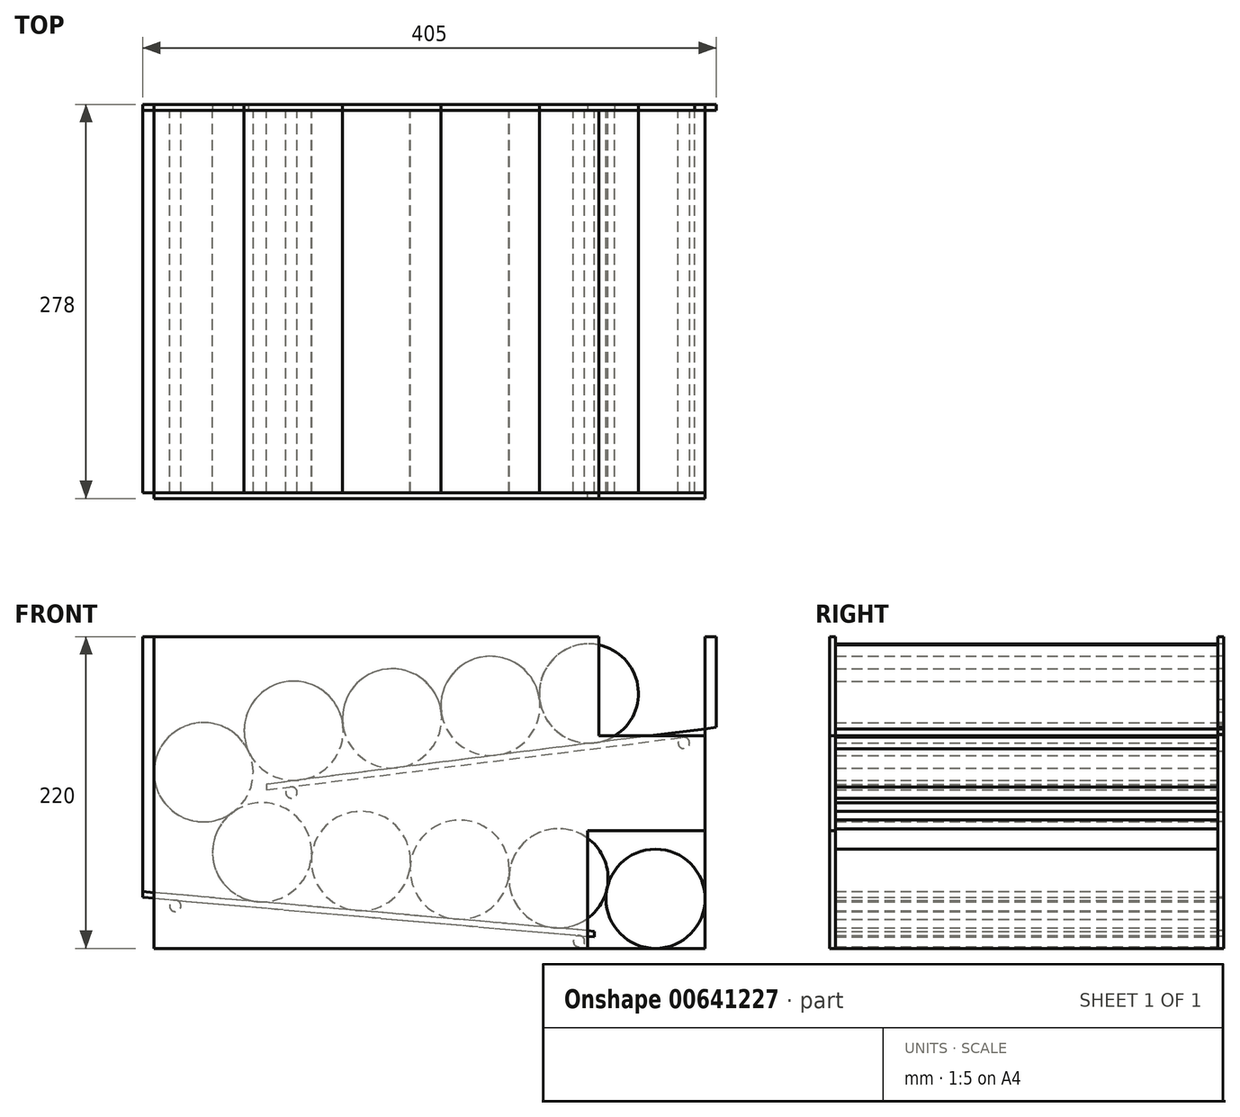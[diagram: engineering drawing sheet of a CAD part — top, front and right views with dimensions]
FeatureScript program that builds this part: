
annotation { "Feature Type Name" : "Feature", "Feature Type Description" : "" }
export const myFeature = defineFeature(function(context is Context, id is Id, definition is map)
    precondition{}
    {
        {
            var Q0;
            Q0=qCreatedBy(makeId("Front.planeOp"),FACE);
            var sketch = newSketch(context, id + "F0", { "sketchPlane" : qUnion([Q0])});
            skLineSegment(sketch, "E0.bottom", {"start": v(0, 0) * mm, "end": v(-405, 0) * mm});
            skLineSegment(sketch, "E0.left", {"start": v(0, 0) * mm, "end": v(0, 84.53) * mm});
            skLineSegment(sketch, "E0.right", {"start": v(-405, 0) * mm, "end": v(-405, 220) * mm});
            skCircle(sketch, "E1", {"center": v(-43, 35) * mm, "radius": 35 * mm});
            skCircle(sketch, "E2", {"center": v(-382, 30) * mm, "radius": 4 * mm});
            skLineSegment(sketch, "E3", {"start": v(-86.22, 12.09) * mm, "end": v(-405, 40.05) * mm});
            skCircle(sketch, "E4", {"center": v(-97, 5) * mm, "radius": 4 * mm});
            skCircle(sketch, "E5", {"center": v(-111.5, 49.44) * mm, "radius": 35 * mm});
            skCircle(sketch, "E6", {"center": v(-181.23, 55.55) * mm, "radius": 35 * mm});
            skCircle(sketch, "E7", {"center": v(-250.96, 61.67) * mm, "radius": 35 * mm});
            skCircle(sketch, "E8", {"center": v(-320.7, 67.79) * mm, "radius": 35 * mm});
            skCircle(sketch, "E9", {"center": v(-362, 124.3) * mm, "radius": 35 * mm});
            skCircle(sketch, "E10", {"center": v(-228.95, 162.32) * mm, "radius": 35 * mm});
            skCircle(sketch, "E11", {"center": v(-298.4, 153.54) * mm, "radius": 35 * mm});
            skLineSegment(sketch, "E12", {"start": v(0, 155.97) * mm, "end": v(-317.48, 115.86) * mm});
            skCircle(sketch, "E13", {"center": v(-23, 145) * mm, "radius": 4 * mm});
            skCircle(sketch, "E14", {"center": v(-300, 110) * mm, "radius": 4 * mm});
            skCircle(sketch, "E15", {"center": v(-159.5, 171.1) * mm, "radius": 35 * mm});
            skCircle(sketch, "E16", {"center": v(-90.06, 179.87) * mm, "radius": 35 * mm});
            skLineSegment(sketch, "E17", {"start": v(-8, 83) * mm, "end": v(-91, 83) * mm});
            skLineSegment(sketch, "E18", {"start": v(-91, 83) * mm, "end": v(-91, 0) * mm});
            skLineSegment(sketch, "E19", {"start": v(-83, 220) * mm, "end": v(-83, 150) * mm});
            skLineSegment(sketch, "E20", {"start": v(-83, 150) * mm, "end": v(0, 150) * mm});
            skLineSegment(sketch, "E21.top", {"start": v(-405, 220) * mm, "end": v(0, 220) * mm});
            skLineSegment(sketch, "E22", {"start": v(-83, 220) * mm, "end": v(0, 220) * mm});
            skLineSegment(sketch, "E23", {"start": v(0, 220) * mm, "end": v(0, 155.97) * mm});
            skLineSegment(sketch, "E24", {"start": v(-317.48, 111.82) * mm, "end": v(0, 151.94) * mm});
            skLineSegment(sketch, "E25", {"start": v(-405, 36.03) * mm, "end": v(-86.22, 8.07) * mm});
            skLineSegment(sketch, "E26", {"start": v(-317.48, 115.86) * mm, "end": v(-317.48, 111.82) * mm});
            skLineSegment(sketch, "E27", {"start": v(-86.22, 12.09) * mm, "end": v(-86.22, 8.07) * mm});
            skLineSegment(sketch, "E28", {"start": v(-397, 220) * mm, "end": v(-397, 0) * mm});
            skLineSegment(sketch, "E29", {"start": v(-8, 220) * mm, "end": v(-8, 0) * mm});
            skSolve(sketch);
        }
        {
            var Q0;
            {var subQ0=sQuery(id+"F0.wireOp",EDGE,"E9");var subQ1=makeQuery(id+"F0.imprint","INTERSECT",VERTEX,{"derivedFrom":[sQuery(id+"F0.wireOp",EDGE,"E0.right"),subQ0]});Q0=makeQuery(id+"F0.imprint","IMPRINT",FACE,{"disambiguationData":[TD([[makeQuery(id+"F0.imprint","IMPRINT",EDGE,{"disambiguationData":[TD([[subQ1,1.0]])],"derivedFrom":subQ0}),1.0]])]});}
            var Q1;
            {var subQ5=sQuery(id+"F0.wireOp",EDGE,"be49a046-d79a-43c6-b33a-aba0699b3afb");var subQ6=sQuery(id+"F0.wireOp",EDGE,"E12");var subQ7=makeQuery(id+"F0.imprint","INTERSECT",VERTEX,{"derivedFrom":[subQ6,subQ5]});Q1=makeQuery(id+"F0.imprint","IMPRINT",FACE,{"disambiguationData":[TD([[makeQuery(id+"F0.imprint","IMPRINT",EDGE,{"disambiguationData":[TD([[subQ7,-1.0]])],"derivedFrom":subQ6}),-1.0]])]});}
            var Q2;
            {var subQ0=sQuery(id+"F0.wireOp",EDGE,"E16");var subQ1=makeQuery(id+"F0.imprint","INTERSECT",VERTEX,{"derivedFrom":[sQuery(id+"F0.wireOp",EDGE,"E15"),subQ0]});Q2=makeQuery(id+"F0.imprint","IMPRINT",FACE,{"disambiguationData":[TD([[makeQuery(id+"F0.imprint","IMPRINT",EDGE,{"disambiguationData":[TD([[subQ1,1.0]])],"derivedFrom":subQ0}),1.0]])]});}
            var Q3;
            {var subQ0=sQuery(id+"F0.wireOp",EDGE,"E16");var subQ1=sQuery(id+"F0.wireOp",EDGE,"E12");var subQ2=makeQuery(id+"F0.imprint","INTERSECT",VERTEX,{"derivedFrom":[subQ1,subQ0]});Q3=makeQuery(id+"F0.imprint","IMPRINT",FACE,{"disambiguationData":[TD([[makeQuery(id+"F0.imprint","IMPRINT",EDGE,{"disambiguationData":[TD([[subQ2,-1.0]])],"derivedFrom":subQ1}),-1.0]])]});}
            var Q4;
            {var subQ0=sQuery(id+"F0.wireOp",EDGE,"E15");var subQ1=makeQuery(id+"F0.imprint","INTERSECT",VERTEX,{"derivedFrom":[sQuery(id+"F0.wireOp",EDGE,"E10"),subQ0]});Q4=makeQuery(id+"F0.imprint","IMPRINT",FACE,{"disambiguationData":[TD([[makeQuery(id+"F0.imprint","IMPRINT",EDGE,{"disambiguationData":[TD([[subQ1,1.0]])],"derivedFrom":subQ0}),1.0]])]});}
            var Q5;
            {var subQ0=sQuery(id+"F0.wireOp",EDGE,"E10");var subQ1=makeQuery(id+"F0.imprint","INTERSECT",VERTEX,{"derivedFrom":[subQ0,sQuery(id+"F0.wireOp",EDGE,"E11")]});Q5=makeQuery(id+"F0.imprint","IMPRINT",FACE,{"disambiguationData":[TD([[makeQuery(id+"F0.imprint","IMPRINT",EDGE,{"disambiguationData":[TD([[subQ1,1.0]])],"derivedFrom":subQ0}),1.0]])]});}
            var Q6;
            {var subQ0=sQuery(id+"F0.wireOp",EDGE,"E11");var subQ1=makeQuery(id+"F0.imprint","INTERSECT",VERTEX,{"derivedFrom":[sQuery(id+"F0.wireOp",EDGE,"E9"),subQ0]});Q6=makeQuery(id+"F0.imprint","IMPRINT",FACE,{"disambiguationData":[TD([[makeQuery(id+"F0.imprint","IMPRINT",EDGE,{"disambiguationData":[TD([[subQ1,1.0]])],"derivedFrom":subQ0}),1.0]])]});}
            var Q7;
            {var subQ0=sQuery(id+"F0.wireOp",EDGE,"E8");var subQ1=makeQuery(id+"F0.imprint","INTERSECT",VERTEX,{"derivedFrom":[sQuery(id+"F0.wireOp",EDGE,"E3"),subQ0]});Q7=makeQuery(id+"F0.imprint","IMPRINT",FACE,{"disambiguationData":[TD([[makeQuery(id+"F0.imprint","IMPRINT",EDGE,{"disambiguationData":[TD([[subQ1,1.0]])],"derivedFrom":subQ0}),1.0]])]});}
            var Q8;
            {var subQ0=sQuery(id+"F0.wireOp",EDGE,"E7");var subQ1=makeQuery(id+"F0.imprint","INTERSECT",VERTEX,{"derivedFrom":[sQuery(id+"F0.wireOp",EDGE,"E3"),subQ0]});Q8=makeQuery(id+"F0.imprint","IMPRINT",FACE,{"disambiguationData":[TD([[makeQuery(id+"F0.imprint","IMPRINT",EDGE,{"disambiguationData":[TD([[subQ1,1.0]])],"derivedFrom":subQ0}),1.0]])]});}
            var Q9;
            {var subQ0=sQuery(id+"F0.wireOp",EDGE,"E6");var subQ1=makeQuery(id+"F0.imprint","INTERSECT",VERTEX,{"derivedFrom":[sQuery(id+"F0.wireOp",EDGE,"E3"),subQ0]});Q9=makeQuery(id+"F0.imprint","IMPRINT",FACE,{"disambiguationData":[TD([[makeQuery(id+"F0.imprint","IMPRINT",EDGE,{"disambiguationData":[TD([[subQ1,1.0]])],"derivedFrom":subQ0}),1.0]])]});}
            var Q10;
            {var subQ0=sQuery(id+"F0.wireOp",EDGE,"E5");var subQ1=makeQuery(id+"F0.imprint","INTERSECT",VERTEX,{"derivedFrom":[subQ0,sQuery(id+"F0.wireOp",EDGE,"E6")]});Q10=makeQuery(id+"F0.imprint","IMPRINT",FACE,{"disambiguationData":[TD([[makeQuery(id+"F0.imprint","IMPRINT",EDGE,{"disambiguationData":[TD([[subQ1,1.0]])],"derivedFrom":subQ0}),1.0]])]});}
            var Q11;
            {var subQ0=sQuery(id+"F0.wireOp",EDGE,"E5");var subQ1=sQuery(id+"F0.wireOp",EDGE,"E3");var subQ2=makeQuery(id+"F0.imprint","INTERSECT",VERTEX,{"derivedFrom":[subQ1,subQ0]});Q11=makeQuery(id+"F0.imprint","IMPRINT",FACE,{"disambiguationData":[TD([[makeQuery(id+"F0.imprint","IMPRINT",EDGE,{"disambiguationData":[TD([[subQ2,-1.0]])],"derivedFrom":subQ1}),-1.0]])]});}
            var Q12;
            {var subQ0=sQuery(id+"F0.wireOp",EDGE,"E6");var subQ1=sQuery(id+"F0.wireOp",EDGE,"E3");var subQ2=makeQuery(id+"F0.imprint","INTERSECT",VERTEX,{"derivedFrom":[subQ1,subQ0]});Q12=makeQuery(id+"F0.imprint","IMPRINT",FACE,{"disambiguationData":[TD([[makeQuery(id+"F0.imprint","IMPRINT",EDGE,{"disambiguationData":[TD([[subQ2,-1.0]])],"derivedFrom":subQ1}),-1.0]])]});}
            var Q13;
            {var subQ0=sQuery(id+"F0.wireOp",EDGE,"E7");var subQ1=sQuery(id+"F0.wireOp",EDGE,"E3");var subQ2=makeQuery(id+"F0.imprint","INTERSECT",VERTEX,{"derivedFrom":[subQ1,subQ0]});Q13=makeQuery(id+"F0.imprint","IMPRINT",FACE,{"disambiguationData":[TD([[makeQuery(id+"F0.imprint","IMPRINT",EDGE,{"disambiguationData":[TD([[subQ2,-1.0]])],"derivedFrom":subQ1}),-1.0]])]});}
            var Q14;
            {var subQ0=sQuery(id+"F0.wireOp",EDGE,"E11");var subQ1=sQuery(id+"F0.wireOp",EDGE,"E10");var subQ2=makeQuery(id+"F0.imprint","INTERSECT",VERTEX,{"derivedFrom":[subQ1,subQ0]});Q14=makeQuery(id+"F0.imprint","IMPRINT",FACE,{"disambiguationData":[TD([[makeQuery(id+"F0.imprint","IMPRINT",EDGE,{"disambiguationData":[TD([[subQ2,-1.0]])],"derivedFrom":subQ1}),-1.0]])]});}
            var Q15;
            {var subQ0=sQuery(id+"F0.wireOp",EDGE,"E15");var subQ1=sQuery(id+"F0.wireOp",EDGE,"E10");var subQ2=makeQuery(id+"F0.imprint","INTERSECT",VERTEX,{"derivedFrom":[subQ1,subQ0]});Q15=makeQuery(id+"F0.imprint","IMPRINT",FACE,{"disambiguationData":[TD([[makeQuery(id+"F0.imprint","IMPRINT",EDGE,{"disambiguationData":[TD([[subQ2,1.0]])],"derivedFrom":subQ1}),-1.0]])]});}
            var Q16;
            {var subQ0=sQuery(id+"F0.wireOp",EDGE,"be49a046-d79a-43c6-b33a-aba0699b3afb");var subQ1=makeQuery(id+"F0.imprint","INTERSECT",VERTEX,{"derivedFrom":[sQuery(id+"F0.wireOp",EDGE,"E12"),subQ0]});Q16=makeQuery(id+"F0.imprint","IMPRINT",FACE,{"disambiguationData":[TD([[makeQuery(id+"F0.imprint","IMPRINT",EDGE,{"disambiguationData":[TD([[subQ1,1.0]])],"derivedFrom":subQ0}),1.0]])]});}
            var Q17;
            {var subQ0=sQuery(id+"F0.wireOp",EDGE,"E3");var subQ1=makeQuery(id+"F0.imprint","INTERSECT",VERTEX,{"derivedFrom":[subQ0,sQuery(id+"F0.wireOp",EDGE,"E4")]});Q17=makeQuery(id+"F0.imprint","IMPRINT",FACE,{"disambiguationData":[TD([[makeQuery(id+"F0.imprint","IMPRINT",EDGE,{"disambiguationData":[TD([[subQ1,1.0]])],"derivedFrom":subQ0}),-1.0]])]});}
            var Q18;
            {var subQ3=sQuery(id+"F0.wireOp",EDGE,"E2");Q18=makeQuery(id+"F0.imprint","IMPRINT",FACE,{"disambiguationData":[TD([[makeQuery(id+"F0.imprint","IMPRINT",EDGE,{"derivedFrom":subQ3}),-1.0]])]});}
            var Q19;
            Q19=makeQuery(id+"F0.imprint","IMPRINT",FACE,{"disambiguationData":[TD([[makeQuery(id+"F0.imprint","IMPRINT",EDGE,{"derivedFrom":sQuery(id+"F0.wireOp",EDGE,"E14")}),1.0]])]});
            var Q20;
            Q20=makeQuery(id+"F0.imprint","IMPRINT",FACE,{"disambiguationData":[TD([[makeQuery(id+"F0.imprint","IMPRINT",EDGE,{"derivedFrom":sQuery(id+"F0.wireOp",EDGE,"E13")}),1.0]])]});
            var Q21;
            {var subQ0=sQuery(id+"F0.wireOp",EDGE,"E12");var subQ1=makeQuery(id+"F0.imprint","INTERSECT",VERTEX,{"derivedFrom":[subQ0,sQuery(id+"F0.wireOp",EDGE,"E13")]});Q21=makeQuery(id+"F0.imprint","IMPRINT",FACE,{"disambiguationData":[TD([[makeQuery(id+"F0.imprint","IMPRINT",EDGE,{"disambiguationData":[TD([[subQ1,1.0]])],"derivedFrom":subQ0}),-1.0]])]});}
            var Q22;
            Q22=makeQuery(id+"F0.imprint","IMPRINT",FACE,{"disambiguationData":[TD([[makeQuery(id+"F0.imprint","IMPRINT",EDGE,{"derivedFrom":sQuery(id+"F0.wireOp",EDGE,"E4")}),1.0]])]});
            var Q23;
            {var subQ1=sQuery(id+"F0.wireOp",EDGE,"E13");Q23=makeQuery(id+"F0.imprint","IMPRINT",FACE,{"disambiguationData":[TD([[makeQuery(id+"F0.imprint","IMPRINT",EDGE,{"derivedFrom":subQ1}),-1.0]])]});}
            var Q24;
            {var subQ5=sQuery(id+"F0.wireOp",EDGE,"E26");Q24=makeQuery(id+"F0.imprint","IMPRINT",FACE,{"disambiguationData":[TD([[makeQuery(id+"F0.imprint","IMPRINT",EDGE,{"derivedFrom":subQ5}),1.0]])]});}
            var Q25;
            {var subQ0=sQuery(id+"F0.wireOp",EDGE,"be49a046-d79a-43c6-b33a-aba0699b3afb");var subQ1=makeQuery(id+"F0.imprint","INTERSECT",VERTEX,{"derivedFrom":[sQuery(id+"F0.wireOp",EDGE,"E16"),subQ0]});Q25=makeQuery(id+"F0.imprint","IMPRINT",FACE,{"disambiguationData":[TD([[makeQuery(id+"F0.imprint","IMPRINT",EDGE,{"disambiguationData":[TD([[subQ1,1.0]])],"derivedFrom":subQ0}),1.0]])]});}
            var Q26;
            {var subQ1=sQuery(id+"F0.wireOp",EDGE,"E9");var subQ9=sQuery(id+"F0.wireOp",EDGE,"E28");var subQ10=makeQuery(id+"F0.imprint","INTERSECT",VERTEX,{"derivedFrom":[subQ1,subQ9]});Q26=makeQuery(id+"F0.imprint","IMPRINT",FACE,{"disambiguationData":[TD([[makeQuery(id+"F0.imprint","IMPRINT",EDGE,{"disambiguationData":[TD([[subQ10,1.0]])],"derivedFrom":subQ1}),-1.0]])]});}
            var Q27;
            {var subQ0=sQuery(id+"F0.wireOp",EDGE,"E8");var subQ1=sQuery(id+"F0.wireOp",EDGE,"E3");var subQ2=makeQuery(id+"F0.imprint","INTERSECT",VERTEX,{"derivedFrom":[subQ1,subQ0]});Q27=makeQuery(id+"F0.imprint","IMPRINT",FACE,{"disambiguationData":[TD([[makeQuery(id+"F0.imprint","IMPRINT",EDGE,{"disambiguationData":[TD([[subQ2,-1.0]])],"derivedFrom":subQ1}),-1.0]])]});}
            var Q28;
            {var subQ0=sQuery(id+"F0.wireOp",EDGE,"E3");var subQ10=sQuery(id+"F0.wireOp",EDGE,"E18");var subQ11=makeQuery(id+"F0.imprint","INTERSECT",VERTEX,{"derivedFrom":[subQ0,subQ10]});Q28=makeQuery(id+"F0.imprint","IMPRINT",FACE,{"disambiguationData":[TD([[makeQuery(id+"F0.imprint","IMPRINT",EDGE,{"disambiguationData":[TD([[subQ11,-1.0]])],"derivedFrom":subQ0}),1.0]])]});}
            var Q29;
            Q29=makeQuery(id+"F0.imprint","IMPRINT",FACE,{"disambiguationData":[TD([[makeQuery(id+"F0.imprint","IMPRINT",EDGE,{"derivedFrom":sQuery(id+"F0.wireOp",EDGE,"E2")}),1.0]])]});
            extrude(context, id + "F1", {"entities" : qUnion([Q0, Q1, Q2, Q3, Q4, Q5, Q6, Q7, Q8, Q9, Q10, Q11, Q12, Q13, Q14, Q15, Q16, Q17, Q18, Q19, Q20, Q21, Q22, Q23, Q24, Q25, Q26, Q27, Q28, Q29]), "depth" : 274 * mm, "offsetDistance" : 25 * mm, "hasSecondDirection" : true, "secondDirectionOppositeDirection" : false, "secondDirectionDepth" : 270 * mm});
        }
        {
            var Q0;
            {var subQ0=sQuery(id+"F0.wireOp",EDGE,"E1");var subQ1=makeQuery(id+"F0.imprint","INTERSECT",VERTEX,{"derivedFrom":[sQuery(id+"F0.wireOp",EDGE,"E0.left"),subQ0]});Q0=makeQuery(id+"F0.imprint","IMPRINT",FACE,{"disambiguationData":[TD([[makeQuery(id+"F0.imprint","IMPRINT",EDGE,{"disambiguationData":[TD([[subQ1,-1.0]])],"derivedFrom":subQ0}),1.0]])]});}
            var Q1;
            {var subQ0=sQuery(id+"F0.wireOp",EDGE,"E5");var subQ1=makeQuery(id+"F0.imprint","INTERSECT",VERTEX,{"derivedFrom":[subQ0,sQuery(id+"F0.wireOp",EDGE,"E6")]});Q1=makeQuery(id+"F0.imprint","IMPRINT",FACE,{"disambiguationData":[TD([[makeQuery(id+"F0.imprint","IMPRINT",EDGE,{"disambiguationData":[TD([[subQ1,1.0]])],"derivedFrom":subQ0}),1.0]])]});}
            var Q2;
            {var subQ0=sQuery(id+"F0.wireOp",EDGE,"E6");var subQ1=makeQuery(id+"F0.imprint","INTERSECT",VERTEX,{"derivedFrom":[sQuery(id+"F0.wireOp",EDGE,"E3"),subQ0]});Q2=makeQuery(id+"F0.imprint","IMPRINT",FACE,{"disambiguationData":[TD([[makeQuery(id+"F0.imprint","IMPRINT",EDGE,{"disambiguationData":[TD([[subQ1,1.0]])],"derivedFrom":subQ0}),1.0]])]});}
            var Q3;
            {var subQ0=sQuery(id+"F0.wireOp",EDGE,"E7");var subQ1=makeQuery(id+"F0.imprint","INTERSECT",VERTEX,{"derivedFrom":[sQuery(id+"F0.wireOp",EDGE,"E3"),subQ0]});Q3=makeQuery(id+"F0.imprint","IMPRINT",FACE,{"disambiguationData":[TD([[makeQuery(id+"F0.imprint","IMPRINT",EDGE,{"disambiguationData":[TD([[subQ1,1.0]])],"derivedFrom":subQ0}),1.0]])]});}
            var Q4;
            {var subQ0=sQuery(id+"F0.wireOp",EDGE,"E8");var subQ1=makeQuery(id+"F0.imprint","INTERSECT",VERTEX,{"derivedFrom":[sQuery(id+"F0.wireOp",EDGE,"E3"),subQ0]});Q4=makeQuery(id+"F0.imprint","IMPRINT",FACE,{"disambiguationData":[TD([[makeQuery(id+"F0.imprint","IMPRINT",EDGE,{"disambiguationData":[TD([[subQ1,1.0]])],"derivedFrom":subQ0}),1.0]])]});}
            var Q5;
            {var subQ0=sQuery(id+"F0.wireOp",EDGE,"E9");var subQ1=makeQuery(id+"F0.imprint","INTERSECT",VERTEX,{"derivedFrom":[sQuery(id+"F0.wireOp",EDGE,"E0.right"),subQ0]});Q5=makeQuery(id+"F0.imprint","IMPRINT",FACE,{"disambiguationData":[TD([[makeQuery(id+"F0.imprint","IMPRINT",EDGE,{"disambiguationData":[TD([[subQ1,1.0]])],"derivedFrom":subQ0}),1.0]])]});}
            var Q6;
            {var subQ0=sQuery(id+"F0.wireOp",EDGE,"E11");var subQ1=makeQuery(id+"F0.imprint","INTERSECT",VERTEX,{"derivedFrom":[sQuery(id+"F0.wireOp",EDGE,"E9"),subQ0]});Q6=makeQuery(id+"F0.imprint","IMPRINT",FACE,{"disambiguationData":[TD([[makeQuery(id+"F0.imprint","IMPRINT",EDGE,{"disambiguationData":[TD([[subQ1,1.0]])],"derivedFrom":subQ0}),1.0]])]});}
            var Q7;
            {var subQ0=sQuery(id+"F0.wireOp",EDGE,"E10");var subQ1=makeQuery(id+"F0.imprint","INTERSECT",VERTEX,{"derivedFrom":[subQ0,sQuery(id+"F0.wireOp",EDGE,"E11")]});Q7=makeQuery(id+"F0.imprint","IMPRINT",FACE,{"disambiguationData":[TD([[makeQuery(id+"F0.imprint","IMPRINT",EDGE,{"disambiguationData":[TD([[subQ1,1.0]])],"derivedFrom":subQ0}),1.0]])]});}
            var Q8;
            {var subQ0=sQuery(id+"F0.wireOp",EDGE,"E15");var subQ1=makeQuery(id+"F0.imprint","INTERSECT",VERTEX,{"derivedFrom":[sQuery(id+"F0.wireOp",EDGE,"E10"),subQ0]});Q8=makeQuery(id+"F0.imprint","IMPRINT",FACE,{"disambiguationData":[TD([[makeQuery(id+"F0.imprint","IMPRINT",EDGE,{"disambiguationData":[TD([[subQ1,1.0]])],"derivedFrom":subQ0}),1.0]])]});}
            var Q9;
            {var subQ0=sQuery(id+"F0.wireOp",EDGE,"E16");var subQ1=makeQuery(id+"F0.imprint","INTERSECT",VERTEX,{"derivedFrom":[sQuery(id+"F0.wireOp",EDGE,"E15"),subQ0]});Q9=makeQuery(id+"F0.imprint","IMPRINT",FACE,{"disambiguationData":[TD([[makeQuery(id+"F0.imprint","IMPRINT",EDGE,{"disambiguationData":[TD([[subQ1,1.0]])],"derivedFrom":subQ0}),1.0]])]});}
            var Q10;
            {var subQ0=sQuery(id+"F0.wireOp",EDGE,"be49a046-d79a-43c6-b33a-aba0699b3afb");var subQ1=makeQuery(id+"F0.imprint","INTERSECT",VERTEX,{"derivedFrom":[sQuery(id+"F0.wireOp",EDGE,"E16"),subQ0]});Q10=makeQuery(id+"F0.imprint","IMPRINT",FACE,{"disambiguationData":[TD([[makeQuery(id+"F0.imprint","IMPRINT",EDGE,{"disambiguationData":[TD([[subQ1,-1.0]])],"derivedFrom":subQ0}),1.0]])]});}
            var Q11;
            {var subQ0=sQuery(id+"F0.wireOp",EDGE,"E5");var subQ1=makeQuery(id+"F0.imprint","INTERSECT",VERTEX,{"derivedFrom":[sQuery(id+"F0.wireOp",EDGE,"E1"),subQ0]});Q11=makeQuery(id+"F0.imprint","IMPRINT",FACE,{"disambiguationData":[TD([[makeQuery(id+"F0.imprint","IMPRINT",EDGE,{"disambiguationData":[TD([[subQ1,1.0]])],"derivedFrom":subQ0}),1.0]])]});}
            var Q12;
            {var subQ0=sQuery(id+"F0.wireOp",EDGE,"E19");var subQ1=sQuery(id+"F0.wireOp",EDGE,"E16");var subQ2=makeQuery(id+"F0.imprint","INTERSECT",VERTEX,{"disambiguationData":[OD(0.0)],"derivedFrom":[subQ1,subQ0]});Q12=makeQuery(id+"F0.imprint","IMPRINT",FACE,{"disambiguationData":[TD([[makeQuery(id+"F0.imprint","IMPRINT",EDGE,{"disambiguationData":[TD([[subQ2,1.0]])],"derivedFrom":subQ1}),1.0]])]});}
            var Q13;
            {var subQ0=sQuery(id+"F0.wireOp",EDGE,"be49a046-d79a-43c6-b33a-aba0699b3afb");var subQ1=makeQuery(id+"F0.imprint","INTERSECT",VERTEX,{"derivedFrom":[sQuery(id+"F0.wireOp",EDGE,"E12"),subQ0]});Q13=makeQuery(id+"F0.imprint","IMPRINT",FACE,{"disambiguationData":[TD([[makeQuery(id+"F0.imprint","IMPRINT",EDGE,{"disambiguationData":[TD([[subQ1,1.0]])],"derivedFrom":subQ0}),1.0]])]});}
            var Q14;
            {var subQ0=sQuery(id+"F0.wireOp",EDGE,"E19");var subQ1=sQuery(id+"F0.wireOp",EDGE,"be49a046-d79a-43c6-b33a-aba0699b3afb");var subQ2=makeQuery(id+"F0.imprint","INTERSECT",VERTEX,{"disambiguationData":[OD(1.0)],"derivedFrom":[subQ1,subQ0]});Q14=makeQuery(id+"F0.imprint","IMPRINT",FACE,{"disambiguationData":[TD([[makeQuery(id+"F0.imprint","IMPRINT",EDGE,{"disambiguationData":[TD([[subQ2,-1.0]])],"derivedFrom":subQ1}),1.0]])]});}
            extrude(context, id + "F2", {"entities" : qUnion([Q0, Q1, Q2, Q3, Q4, Q5, Q6, Q7, Q8, Q9, Q10, Q11, Q12, Q13, Q14]), "depth" : 270 * mm, "offsetDistance" : 25 * mm});
        }
        {
            var Q0;
            Q0=makeQuery(id+"F0.imprint","IMPRINT",FACE,{"disambiguationData":[TD([[makeQuery(id+"F0.imprint","IMPRINT",EDGE,{"derivedFrom":sQuery(id+"F0.wireOp",EDGE,"E14")}),1.0]])]});
            var Q1;
            Q1=makeQuery(id+"F0.imprint","IMPRINT",FACE,{"disambiguationData":[TD([[makeQuery(id+"F0.imprint","IMPRINT",EDGE,{"derivedFrom":sQuery(id+"F0.wireOp",EDGE,"E2")}),1.0]])]});
            var Q2;
            Q2=makeQuery(id+"F0.imprint","IMPRINT",FACE,{"disambiguationData":[TD([[makeQuery(id+"F0.imprint","IMPRINT",EDGE,{"derivedFrom":sQuery(id+"F0.wireOp",EDGE,"E13")}),1.0]])]});
            var Q3;
            Q3=makeQuery(id+"F0.imprint","IMPRINT",FACE,{"disambiguationData":[TD([[makeQuery(id+"F0.imprint","IMPRINT",EDGE,{"derivedFrom":sQuery(id+"F0.wireOp",EDGE,"E4")}),1.0]])]});
            extrude(context, id + "F3", {"entities" : qUnion([Q0, Q1, Q2, Q3]), "depth" : 270 * mm, "offsetDistance" : 25 * mm});
        }
        {
            var Q0;
            {var subQ0=sQuery(id+"F0.wireOp",EDGE,"E3");var subQ6=sQuery(id+"F0.wireOp",EDGE,"E0.right");var subQ7=makeQuery(id+"F0.imprint","INTERSECT",VERTEX,{"derivedFrom":[subQ6,subQ0]});Q0=makeQuery(id+"F0.imprint","IMPRINT",FACE,{"disambiguationData":[TD([[makeQuery(id+"F0.imprint","IMPRINT",EDGE,{"disambiguationData":[TD([[subQ7,1.0]])],"derivedFrom":subQ6}),-1.0]])]});}
            var Q1;
            {var subQ1=sQuery(id+"F0.wireOp",EDGE,"E0.left");var subQ3=sQuery(id+"F0.wireOp",EDGE,"E20");var subQ4=makeQuery(id+"F0.imprint","INTERSECT",VERTEX,{"derivedFrom":[subQ1,subQ3]});Q1=makeQuery(id+"F0.imprint","IMPRINT",FACE,{"disambiguationData":[TD([[makeQuery(id+"F0.imprint","IMPRINT",EDGE,{"disambiguationData":[TD([[subQ4,1.0]])],"derivedFrom":subQ3}),1.0]])]});}
            var Q2;
            {var subQ0=sQuery(id+"F0.wireOp",EDGE,"E26");Q2=makeQuery(id+"F0.imprint","IMPRINT",FACE,{"disambiguationData":[TD([[makeQuery(id+"F0.imprint","IMPRINT",EDGE,{"derivedFrom":subQ0}),1.0]])]});}
            var Q3;
            {var subQ0=sQuery(id+"F0.wireOp",EDGE,"E29");var subQ1=sQuery(id+"F0.wireOp",EDGE,"E12");var subQ2=makeQuery(id+"F0.imprint","INTERSECT",VERTEX,{"derivedFrom":[subQ1,subQ0]});Q3=makeQuery(id+"F0.imprint","IMPRINT",FACE,{"disambiguationData":[TD([[makeQuery(id+"F0.imprint","IMPRINT",EDGE,{"disambiguationData":[TD([[subQ2,-1.0]])],"derivedFrom":subQ1}),1.0]])]});}
            var Q4;
            {var subQ0=sQuery(id+"F0.wireOp",EDGE,"E3");var subQ10=sQuery(id+"F0.wireOp",EDGE,"E18");var subQ11=makeQuery(id+"F0.imprint","INTERSECT",VERTEX,{"derivedFrom":[subQ0,subQ10]});Q4=makeQuery(id+"F0.imprint","IMPRINT",FACE,{"disambiguationData":[TD([[makeQuery(id+"F0.imprint","IMPRINT",EDGE,{"disambiguationData":[TD([[subQ11,-1.0]])],"derivedFrom":subQ0}),1.0]])]});}
            var Q5;
            {var subQ0=sQuery(id+"F0.wireOp",EDGE,"E27");Q5=makeQuery(id+"F0.imprint","IMPRINT",FACE,{"disambiguationData":[TD([[makeQuery(id+"F0.imprint","IMPRINT",EDGE,{"derivedFrom":subQ0}),-1.0]])]});}
            var Q6;
            {var subQ0=sQuery(id+"F0.wireOp",EDGE,"E20");var subQ1=sQuery(id+"F0.wireOp",EDGE,"E0.left");var subQ2=makeQuery(id+"F0.imprint","INTERSECT",VERTEX,{"derivedFrom":[subQ1,subQ0]});Q6=makeQuery(id+"F0.imprint","IMPRINT",FACE,{"disambiguationData":[TD([[makeQuery(id+"F0.imprint","IMPRINT",EDGE,{"disambiguationData":[TD([[subQ2,1.0]])],"derivedFrom":subQ1}),1.0]])]});}
            extrude(context, id + "F4", {"entities" : qUnion([Q0, Q1, Q2, Q3, Q4, Q5, Q6]), "depth" : 270 * mm, "offsetDistance" : 25 * mm});
        }
        {
            var Q0;
            {var subQ7=sQuery(id+"F0.wireOp",EDGE,"E21.top");Q0=makeQuery(id+"F0.imprint","IMPRINT",FACE,{"disambiguationData":[TD([[makeQuery(id+"F0.imprint","IMPRINT",EDGE,{"derivedFrom":subQ7}),-1.0]])]});}
            var Q1;
            {var subQ5=sQuery(id+"F0.wireOp",EDGE,"E22");Q1=makeQuery(id+"F0.imprint","IMPRINT",FACE,{"disambiguationData":[TD([[makeQuery(id+"F0.imprint","IMPRINT",EDGE,{"derivedFrom":subQ5}),-1.0]])]});}
            var Q2;
            {var subQ0=sQuery(id+"F0.wireOp",EDGE,"E19");var subQ1=sQuery(id+"F0.wireOp",EDGE,"be49a046-d79a-43c6-b33a-aba0699b3afb");var subQ2=makeQuery(id+"F0.imprint","INTERSECT",VERTEX,{"disambiguationData":[OD(1.0)],"derivedFrom":[subQ1,subQ0]});Q2=makeQuery(id+"F0.imprint","IMPRINT",FACE,{"disambiguationData":[TD([[makeQuery(id+"F0.imprint","IMPRINT",EDGE,{"disambiguationData":[TD([[subQ2,-1.0]])],"derivedFrom":subQ1}),1.0]])]});}
            var Q3;
            {var subQ0=sQuery(id+"F0.wireOp",EDGE,"E19");var subQ1=sQuery(id+"F0.wireOp",EDGE,"be49a046-d79a-43c6-b33a-aba0699b3afb");var subQ2=makeQuery(id+"F0.imprint","INTERSECT",VERTEX,{"disambiguationData":[OD(1.0)],"derivedFrom":[subQ1,subQ0]});Q3=makeQuery(id+"F0.imprint","IMPRINT",FACE,{"disambiguationData":[TD([[makeQuery(id+"F0.imprint","IMPRINT",EDGE,{"disambiguationData":[TD([[subQ2,-1.0]])],"derivedFrom":subQ1}),-1.0]])]});}
            var Q4;
            {var subQ0=sQuery(id+"F0.wireOp",EDGE,"be49a046-d79a-43c6-b33a-aba0699b3afb");var subQ1=sQuery(id+"F0.wireOp",EDGE,"E12");var subQ2=makeQuery(id+"F0.imprint","INTERSECT",VERTEX,{"derivedFrom":[subQ1,subQ0]});Q4=makeQuery(id+"F0.imprint","IMPRINT",FACE,{"disambiguationData":[TD([[makeQuery(id+"F0.imprint","IMPRINT",EDGE,{"disambiguationData":[TD([[subQ2,-1.0]])],"derivedFrom":subQ1}),-1.0]])]});}
            var Q5;
            {var subQ0=sQuery(id+"F0.wireOp",EDGE,"E16");var subQ1=sQuery(id+"F0.wireOp",EDGE,"E12");var subQ2=makeQuery(id+"F0.imprint","INTERSECT",VERTEX,{"derivedFrom":[subQ1,subQ0]});Q5=makeQuery(id+"F0.imprint","IMPRINT",FACE,{"disambiguationData":[TD([[makeQuery(id+"F0.imprint","IMPRINT",EDGE,{"disambiguationData":[TD([[subQ2,-1.0]])],"derivedFrom":subQ1}),-1.0]])]});}
            var Q6;
            {var subQ0=sQuery(id+"F0.wireOp",EDGE,"E15");var subQ1=makeQuery(id+"F0.imprint","INTERSECT",VERTEX,{"derivedFrom":[sQuery(id+"F0.wireOp",EDGE,"E10"),subQ0]});Q6=makeQuery(id+"F0.imprint","IMPRINT",FACE,{"disambiguationData":[TD([[makeQuery(id+"F0.imprint","IMPRINT",EDGE,{"disambiguationData":[TD([[subQ1,1.0]])],"derivedFrom":subQ0}),1.0]])]});}
            var Q7;
            {var subQ0=sQuery(id+"F0.wireOp",EDGE,"E15");var subQ1=sQuery(id+"F0.wireOp",EDGE,"E10");var subQ2=makeQuery(id+"F0.imprint","INTERSECT",VERTEX,{"derivedFrom":[subQ1,subQ0]});Q7=makeQuery(id+"F0.imprint","IMPRINT",FACE,{"disambiguationData":[TD([[makeQuery(id+"F0.imprint","IMPRINT",EDGE,{"disambiguationData":[TD([[subQ2,1.0]])],"derivedFrom":subQ1}),-1.0]])]});}
            var Q8;
            {var subQ0=sQuery(id+"F0.wireOp",EDGE,"E10");var subQ1=makeQuery(id+"F0.imprint","INTERSECT",VERTEX,{"derivedFrom":[subQ0,sQuery(id+"F0.wireOp",EDGE,"E11")]});Q8=makeQuery(id+"F0.imprint","IMPRINT",FACE,{"disambiguationData":[TD([[makeQuery(id+"F0.imprint","IMPRINT",EDGE,{"disambiguationData":[TD([[subQ1,1.0]])],"derivedFrom":subQ0}),1.0]])]});}
            var Q9;
            {var subQ0=sQuery(id+"F0.wireOp",EDGE,"E11");var subQ1=sQuery(id+"F0.wireOp",EDGE,"E10");var subQ2=makeQuery(id+"F0.imprint","INTERSECT",VERTEX,{"derivedFrom":[subQ1,subQ0]});Q9=makeQuery(id+"F0.imprint","IMPRINT",FACE,{"disambiguationData":[TD([[makeQuery(id+"F0.imprint","IMPRINT",EDGE,{"disambiguationData":[TD([[subQ2,-1.0]])],"derivedFrom":subQ1}),-1.0]])]});}
            var Q10;
            {var subQ0=sQuery(id+"F0.wireOp",EDGE,"E11");var subQ1=makeQuery(id+"F0.imprint","INTERSECT",VERTEX,{"derivedFrom":[sQuery(id+"F0.wireOp",EDGE,"E9"),subQ0]});Q10=makeQuery(id+"F0.imprint","IMPRINT",FACE,{"disambiguationData":[TD([[makeQuery(id+"F0.imprint","IMPRINT",EDGE,{"disambiguationData":[TD([[subQ1,1.0]])],"derivedFrom":subQ0}),1.0]])]});}
            var Q11;
            {var subQ0=sQuery(id+"F0.wireOp",EDGE,"E9");var subQ1=makeQuery(id+"F0.imprint","INTERSECT",VERTEX,{"derivedFrom":[sQuery(id+"F0.wireOp",EDGE,"E0.right"),subQ0]});Q11=makeQuery(id+"F0.imprint","IMPRINT",FACE,{"disambiguationData":[TD([[makeQuery(id+"F0.imprint","IMPRINT",EDGE,{"disambiguationData":[TD([[subQ1,1.0]])],"derivedFrom":subQ0}),1.0]])]});}
            var Q12;
            {var subQ0=sQuery(id+"F0.wireOp",EDGE,"E3");var subQ1=sQuery(id+"F0.wireOp",EDGE,"E0.right");var subQ2=makeQuery(id+"F0.imprint","INTERSECT",VERTEX,{"derivedFrom":[subQ1,subQ0]});Q12=makeQuery(id+"F0.imprint","IMPRINT",FACE,{"disambiguationData":[TD([[makeQuery(id+"F0.imprint","IMPRINT",EDGE,{"disambiguationData":[TD([[subQ2,-1.0]])],"derivedFrom":subQ1}),-1.0]])]});}
            var Q13;
            {var subQ5=sQuery(id+"F0.wireOp",EDGE,"E26");Q13=makeQuery(id+"F0.imprint","IMPRINT",FACE,{"disambiguationData":[TD([[makeQuery(id+"F0.imprint","IMPRINT",EDGE,{"derivedFrom":subQ5}),1.0]])]});}
            var Q14;
            Q14=makeQuery(id+"F0.imprint","IMPRINT",FACE,{"disambiguationData":[TD([[makeQuery(id+"F0.imprint","IMPRINT",EDGE,{"derivedFrom":sQuery(id+"F0.wireOp",EDGE,"E14")}),1.0]])]});
            var Q15;
            Q15=makeQuery(id+"F0.imprint","IMPRINT",FACE,{"disambiguationData":[TD([[makeQuery(id+"F0.imprint","IMPRINT",EDGE,{"derivedFrom":sQuery(id+"F0.wireOp",EDGE,"E13")}),1.0]])]});
            var Q16;
            {var subQ0=sQuery(id+"F0.wireOp",EDGE,"E17");Q16=makeQuery(id+"F0.imprint","IMPRINT",FACE,{"disambiguationData":[TD([[makeQuery(id+"F0.imprint","IMPRINT",EDGE,{"derivedFrom":subQ0}),1.0]])]});}
            var Q17;
            {var subQ0=sQuery(id+"F0.wireOp",EDGE,"E1");var subQ1=makeQuery(id+"F0.imprint","INTERSECT",VERTEX,{"derivedFrom":[sQuery(id+"F0.wireOp",EDGE,"E0.left"),subQ0]});Q17=makeQuery(id+"F0.imprint","IMPRINT",FACE,{"disambiguationData":[TD([[makeQuery(id+"F0.imprint","IMPRINT",EDGE,{"disambiguationData":[TD([[subQ1,-1.0]])],"derivedFrom":subQ0}),1.0]])]});}
            var Q18;
            {var subQ0=sQuery(id+"F0.wireOp",EDGE,"E0.left");var subQ1=sQuery(id+"F0.wireOp",EDGE,"E0.bottom");var subQ2=makeQuery(id+"F0.imprint","INTERSECT",VERTEX,{"derivedFrom":[subQ1,subQ0]});Q18=makeQuery(id+"F0.imprint","IMPRINT",FACE,{"disambiguationData":[TD([[makeQuery(id+"F0.imprint","IMPRINT",EDGE,{"disambiguationData":[TD([[subQ2,-1.0]])],"derivedFrom":subQ1}),-1.0]])]});}
            var Q19;
            {var subQ9=sQuery(id+"F0.wireOp",EDGE,"E27");Q19=makeQuery(id+"F0.imprint","IMPRINT",FACE,{"disambiguationData":[TD([[makeQuery(id+"F0.imprint","IMPRINT",EDGE,{"derivedFrom":subQ9}),1.0]])]});}
            var Q20;
            {var subQ0=sQuery(id+"F0.wireOp",EDGE,"E5");var subQ1=sQuery(id+"F0.wireOp",EDGE,"E3");var subQ2=makeQuery(id+"F0.imprint","INTERSECT",VERTEX,{"derivedFrom":[subQ1,subQ0]});Q20=makeQuery(id+"F0.imprint","IMPRINT",FACE,{"disambiguationData":[TD([[makeQuery(id+"F0.imprint","IMPRINT",EDGE,{"disambiguationData":[TD([[subQ2,-1.0]])],"derivedFrom":subQ1}),-1.0]])]});}
            var Q21;
            {var subQ0=sQuery(id+"F0.wireOp",EDGE,"E5");var subQ1=makeQuery(id+"F0.imprint","INTERSECT",VERTEX,{"derivedFrom":[subQ0,sQuery(id+"F0.wireOp",EDGE,"E6")]});Q21=makeQuery(id+"F0.imprint","IMPRINT",FACE,{"disambiguationData":[TD([[makeQuery(id+"F0.imprint","IMPRINT",EDGE,{"disambiguationData":[TD([[subQ1,1.0]])],"derivedFrom":subQ0}),1.0]])]});}
            var Q22;
            {var subQ0=sQuery(id+"F0.wireOp",EDGE,"E6");var subQ1=makeQuery(id+"F0.imprint","INTERSECT",VERTEX,{"derivedFrom":[sQuery(id+"F0.wireOp",EDGE,"E3"),subQ0]});Q22=makeQuery(id+"F0.imprint","IMPRINT",FACE,{"disambiguationData":[TD([[makeQuery(id+"F0.imprint","IMPRINT",EDGE,{"disambiguationData":[TD([[subQ1,1.0]])],"derivedFrom":subQ0}),1.0]])]});}
            var Q23;
            {var subQ0=sQuery(id+"F0.wireOp",EDGE,"E5");var subQ1=makeQuery(id+"F0.imprint","INTERSECT",VERTEX,{"derivedFrom":[sQuery(id+"F0.wireOp",EDGE,"E1"),subQ0]});Q23=makeQuery(id+"F0.imprint","IMPRINT",FACE,{"disambiguationData":[TD([[makeQuery(id+"F0.imprint","IMPRINT",EDGE,{"disambiguationData":[TD([[subQ1,1.0]])],"derivedFrom":subQ0}),1.0]])]});}
            var Q24;
            {var subQ0=sQuery(id+"F0.wireOp",EDGE,"E7");var subQ1=makeQuery(id+"F0.imprint","INTERSECT",VERTEX,{"derivedFrom":[sQuery(id+"F0.wireOp",EDGE,"E3"),subQ0]});Q24=makeQuery(id+"F0.imprint","IMPRINT",FACE,{"disambiguationData":[TD([[makeQuery(id+"F0.imprint","IMPRINT",EDGE,{"disambiguationData":[TD([[subQ1,1.0]])],"derivedFrom":subQ0}),1.0]])]});}
            var Q25;
            {var subQ0=sQuery(id+"F0.wireOp",EDGE,"E7");var subQ1=sQuery(id+"F0.wireOp",EDGE,"E3");var subQ2=makeQuery(id+"F0.imprint","INTERSECT",VERTEX,{"derivedFrom":[subQ1,subQ0]});Q25=makeQuery(id+"F0.imprint","IMPRINT",FACE,{"disambiguationData":[TD([[makeQuery(id+"F0.imprint","IMPRINT",EDGE,{"disambiguationData":[TD([[subQ2,-1.0]])],"derivedFrom":subQ1}),-1.0]])]});}
            var Q26;
            {var subQ0=sQuery(id+"F0.wireOp",EDGE,"E6");var subQ1=sQuery(id+"F0.wireOp",EDGE,"E3");var subQ2=makeQuery(id+"F0.imprint","INTERSECT",VERTEX,{"derivedFrom":[subQ1,subQ0]});Q26=makeQuery(id+"F0.imprint","IMPRINT",FACE,{"disambiguationData":[TD([[makeQuery(id+"F0.imprint","IMPRINT",EDGE,{"disambiguationData":[TD([[subQ2,-1.0]])],"derivedFrom":subQ1}),-1.0]])]});}
            var Q27;
            {var subQ0=sQuery(id+"F0.wireOp",EDGE,"E2");Q27=makeQuery(id+"F0.imprint","IMPRINT",FACE,{"disambiguationData":[TD([[makeQuery(id+"F0.imprint","IMPRINT",EDGE,{"derivedFrom":subQ0}),-1.0]])]});}
            var Q28;
            Q28=makeQuery(id+"F0.imprint","IMPRINT",FACE,{"disambiguationData":[TD([[makeQuery(id+"F0.imprint","IMPRINT",EDGE,{"derivedFrom":sQuery(id+"F0.wireOp",EDGE,"E4")}),1.0]])]});
            var Q29;
            Q29=makeQuery(id+"F0.imprint","IMPRINT",FACE,{"disambiguationData":[TD([[makeQuery(id+"F0.imprint","IMPRINT",EDGE,{"derivedFrom":sQuery(id+"F0.wireOp",EDGE,"E2")}),1.0]])]});
            var Q30;
            {var subQ0=sQuery(id+"F0.wireOp",EDGE,"E3");var subQ6=sQuery(id+"F0.wireOp",EDGE,"E0.right");var subQ7=makeQuery(id+"F0.imprint","INTERSECT",VERTEX,{"derivedFrom":[subQ6,subQ0]});Q30=makeQuery(id+"F0.imprint","IMPRINT",FACE,{"disambiguationData":[TD([[makeQuery(id+"F0.imprint","IMPRINT",EDGE,{"disambiguationData":[TD([[subQ7,1.0]])],"derivedFrom":subQ6}),-1.0]])]});}
            var Q31;
            {var subQ1=sQuery(id+"F0.wireOp",EDGE,"E13");Q31=makeQuery(id+"F0.imprint","IMPRINT",FACE,{"disambiguationData":[TD([[makeQuery(id+"F0.imprint","IMPRINT",EDGE,{"derivedFrom":subQ1}),-1.0]])]});}
            var Q32;
            {var subQ0=sQuery(id+"F0.wireOp",EDGE,"E18");var subQ1=sQuery(id+"F0.wireOp",EDGE,"E3");var subQ2=makeQuery(id+"F0.imprint","INTERSECT",VERTEX,{"derivedFrom":[subQ1,subQ0]});Q32=makeQuery(id+"F0.imprint","IMPRINT",FACE,{"disambiguationData":[TD([[makeQuery(id+"F0.imprint","IMPRINT",EDGE,{"disambiguationData":[TD([[subQ2,-1.0]])],"derivedFrom":subQ1}),-1.0]])]});}
            var Q33;
            {var subQ0=sQuery(id+"F0.wireOp",EDGE,"E27");Q33=makeQuery(id+"F0.imprint","IMPRINT",FACE,{"disambiguationData":[TD([[makeQuery(id+"F0.imprint","IMPRINT",EDGE,{"derivedFrom":subQ0}),-1.0]])]});}
            var Q34;
            {var subQ0=sQuery(id+"F0.wireOp",EDGE,"be49a046-d79a-43c6-b33a-aba0699b3afb");var subQ1=makeQuery(id+"F0.imprint","INTERSECT",VERTEX,{"derivedFrom":[sQuery(id+"F0.wireOp",EDGE,"E12"),subQ0]});Q34=makeQuery(id+"F0.imprint","IMPRINT",FACE,{"disambiguationData":[TD([[makeQuery(id+"F0.imprint","IMPRINT",EDGE,{"disambiguationData":[TD([[subQ1,1.0]])],"derivedFrom":subQ0}),1.0]])]});}
            var Q35;
            {var subQ0=sQuery(id+"F0.wireOp",EDGE,"E20");var subQ1=sQuery(id+"F0.wireOp",EDGE,"E12");var subQ2=makeQuery(id+"F0.imprint","INTERSECT",VERTEX,{"derivedFrom":[subQ1,subQ0]});Q35=makeQuery(id+"F0.imprint","IMPRINT",FACE,{"disambiguationData":[TD([[makeQuery(id+"F0.imprint","IMPRINT",EDGE,{"disambiguationData":[TD([[subQ2,-1.0]])],"derivedFrom":subQ1}),-1.0]])]});}
            var Q36;
            {var subQ1=sQuery(id+"F0.wireOp",EDGE,"E0.left");var subQ3=sQuery(id+"F0.wireOp",EDGE,"E20");var subQ4=makeQuery(id+"F0.imprint","INTERSECT",VERTEX,{"derivedFrom":[subQ1,subQ3]});Q36=makeQuery(id+"F0.imprint","IMPRINT",FACE,{"disambiguationData":[TD([[makeQuery(id+"F0.imprint","IMPRINT",EDGE,{"disambiguationData":[TD([[subQ4,1.0]])],"derivedFrom":subQ3}),1.0]])]});}
            var Q37;
            {var subQ0=sQuery(id+"F0.wireOp",EDGE,"be49a046-d79a-43c6-b33a-aba0699b3afb");var subQ1=makeQuery(id+"F0.imprint","INTERSECT",VERTEX,{"derivedFrom":[sQuery(id+"F0.wireOp",EDGE,"E16"),subQ0]});Q37=makeQuery(id+"F0.imprint","IMPRINT",FACE,{"disambiguationData":[TD([[makeQuery(id+"F0.imprint","IMPRINT",EDGE,{"disambiguationData":[TD([[subQ1,1.0]])],"derivedFrom":subQ0}),1.0]])]});}
            var Q38;
            {var subQ0=sQuery(id+"F0.wireOp",EDGE,"E16");var subQ1=makeQuery(id+"F0.imprint","INTERSECT",VERTEX,{"derivedFrom":[sQuery(id+"F0.wireOp",EDGE,"E15"),subQ0]});Q38=makeQuery(id+"F0.imprint","IMPRINT",FACE,{"disambiguationData":[TD([[makeQuery(id+"F0.imprint","IMPRINT",EDGE,{"disambiguationData":[TD([[subQ1,1.0]])],"derivedFrom":subQ0}),1.0]])]});}
            var Q39;
            {var subQ0=sQuery(id+"F0.wireOp",EDGE,"E8");var subQ1=makeQuery(id+"F0.imprint","INTERSECT",VERTEX,{"derivedFrom":[sQuery(id+"F0.wireOp",EDGE,"E3"),subQ0]});Q39=makeQuery(id+"F0.imprint","IMPRINT",FACE,{"disambiguationData":[TD([[makeQuery(id+"F0.imprint","IMPRINT",EDGE,{"disambiguationData":[TD([[subQ1,1.0]])],"derivedFrom":subQ0}),1.0]])]});}
            extrude(context, id + "F5", {"entities" : qUnion([Q0, Q1, Q2, Q3, Q4, Q5, Q6, Q7, Q8, Q9, Q10, Q11, Q12, Q13, Q14, Q15, Q16, Q17, Q18, Q19, Q20, Q21, Q22, Q23, Q24, Q25, Q26, Q27, Q28, Q29, Q30, Q31, Q32, Q33, Q34, Q35, Q36, Q37, Q38, Q39]), "oppositeDirection" : true, "depth" : 4 * mm, "offsetDistance" : 25 * mm});
        }
    });
